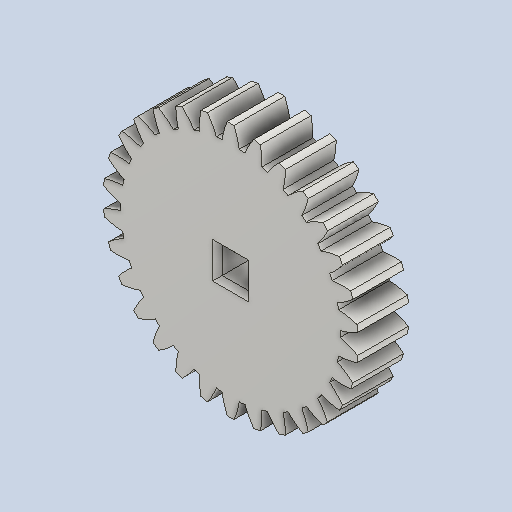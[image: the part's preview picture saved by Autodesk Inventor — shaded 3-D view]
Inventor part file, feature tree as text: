
AUTODESK INVENTOR PART (.ipt)
format: ipt  version: 2022 (Build 260153000, 153)  size: 348,160 bytes
history: native  units: in
note: dims shown in document units (in); Inventor stores cm internally (conversion verified against a paired STEP export)
features: other x12, sketch x3, plane x3
ambient origin geometry x8: Origin, YZ Plane, XZ Plane, XY Plane, X Axis, Y Axis, Z Axis, Center Point
bodies: Solid1 (feature_tree)
feature tree (18):
  other  "Spur Gear14_MIR.ipt"
  other  "Solid1::Spur Gear14_MIR.ipt"
  other  "TaggingFeature1"
  sketch  "Sketch1"  dims[d0=0.3937in]
  sketch  "Sketch2"  dims[d9=0.0in d14=0.0in d15=1.0in d16=0.0in d17=0.0in d18=0.0in d19=1.0in]
  sketch  "Sketch3"
  plane  "XZ Plane_1"
  plane  "Work Plane2"
  plane  "Work Plane3"
  other  "Srf1"
  other  "Srf1::Derived"
  other  "Start plane iMate"
  other  "Distance iMate"
  other  "Position iMate"
  other  "Mesh iMate"
  other  "Axis iMate"
  other  "Mesh iMate2"
  other  "Align iMate"
